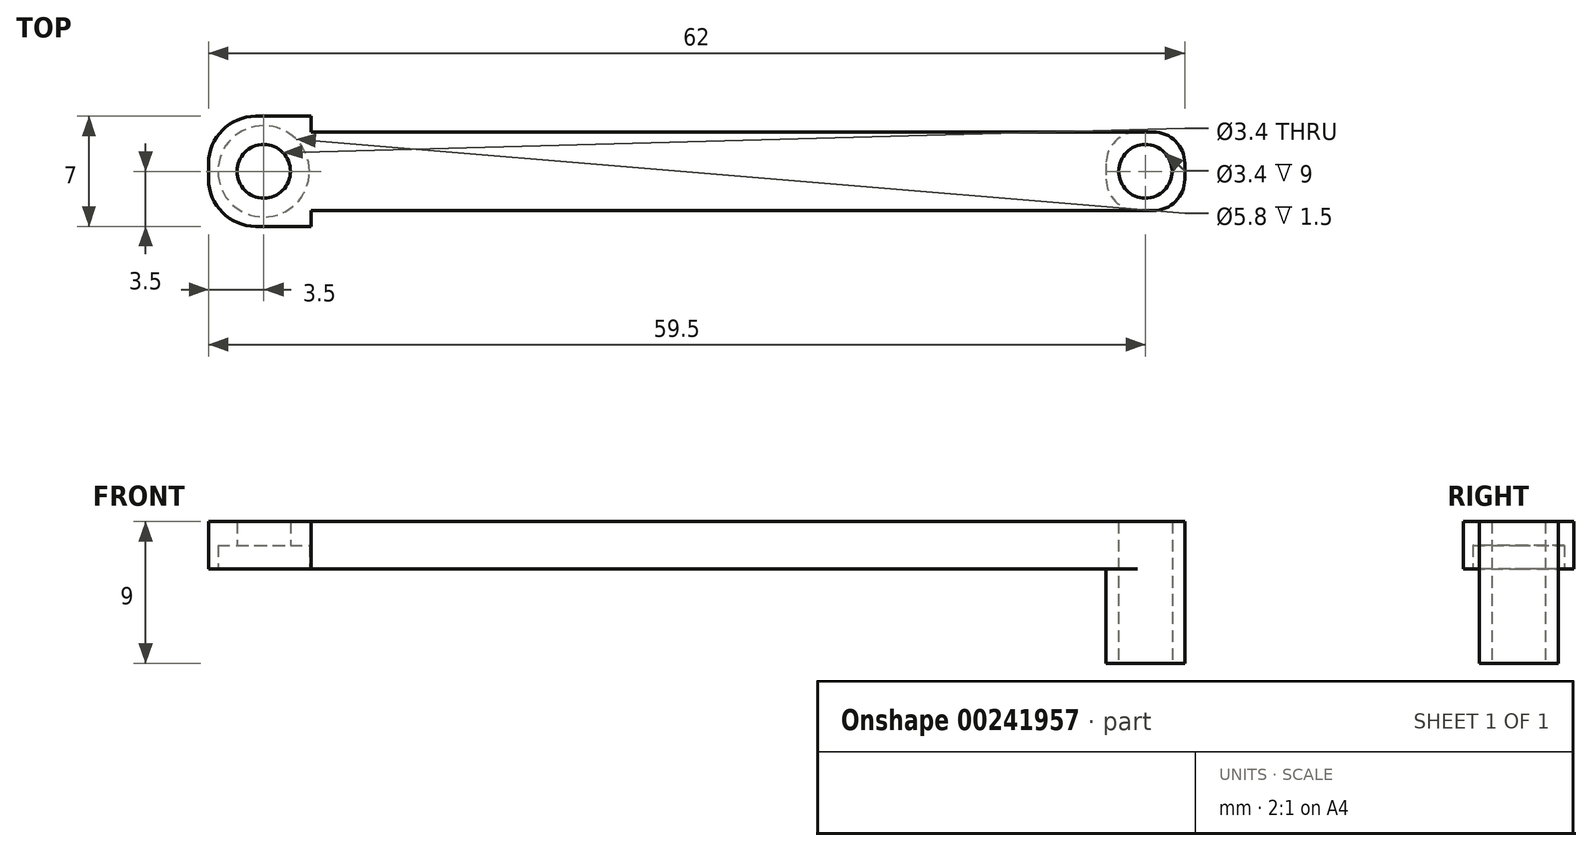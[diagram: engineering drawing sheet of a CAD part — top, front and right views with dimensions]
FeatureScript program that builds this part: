
annotation { "Feature Type Name" : "Feature", "Feature Type Description" : "" }
export const myFeature = defineFeature(function(context is Context, id is Id, definition is map)
    precondition{}
    {
        {
            var Q0;
            Q0=qCreatedBy(makeId("Top.planeOp"),FACE);
            var sketch = newSketch(context, id + "F0", { "sketchPlane" : qUnion([Q0])});
            skCircle(sketch, "E0", {"center": v(0, 0) * mm, "radius": 1.7 * mm});
            skCircle(sketch, "E1", {"center": v(56, 0) * mm, "radius": 1.7 * mm});
            skLineSegment(sketch, "E2", {"start": v(0, 0) * mm, "end": v(56, 0) * mm, "construction": true});
            skLineSegment(sketch, "E3", {"start": v(-2.5, 0) * mm, "end": v(-2.5, 2.5) * mm});
            skLineSegment(sketch, "E4", {"start": v(-2.5, 2.5) * mm, "end": v(58.5, 2.5) * mm});
            skLineSegment(sketch, "E5", {"start": v(58.5, 2.5) * mm, "end": v(58.5, 0) * mm});
            skLineSegment(sketch, "E6.MirrorCS", {"start": v(-2.5, 0) * mm, "end": v(-2.5, -2.5) * mm});
            skLineSegment(sketch, "E7.MirrorCS", {"start": v(-2.5, -2.5) * mm, "end": v(58.5, -2.5) * mm});
            skLineSegment(sketch, "E8.MirrorCS", {"start": v(58.5, -2.5) * mm, "end": v(58.5, 0) * mm});
            skSolve(sketch);
        }
        {
            var Q0;
            Q0=makeQuery(id+"F0.imprint","IMPRINT",FACE,{"disambiguationData":[TD([[makeQuery(id+"F0.imprint","IMPRINT",EDGE,{"derivedFrom":sQuery(id+"F0.wireOp",EDGE,"E0")}),-1.0]])]});
            extrude(context, id + "F1", {"entities" : qUnion([Q0]), "depth" : 3 * mm});
        }
        {
            var Q0;
            Q0=makeQuery(id+"F1.opExtrude","SWEPT_EDGE",EDGE,{"disambiguationData":[OSD([sQuery(id+"F0.wireOp",EDGE,"E3"),sQuery(id+"F0.wireOp",EDGE,"E4")])]});
            var Q1;
            Q1=makeQuery(id+"F1.opExtrude","SWEPT_EDGE",EDGE,{"disambiguationData":[OSD([sQuery(id+"F0.wireOp",EDGE,"E6.MirrorCS"),sQuery(id+"F0.wireOp",EDGE,"E7.MirrorCS")])]});
            var Q2;
            Q2=makeQuery(id+"F1.opExtrude","SWEPT_EDGE",EDGE,{"disambiguationData":[OSD([sQuery(id+"F0.wireOp",EDGE,"E4"),sQuery(id+"F0.wireOp",EDGE,"E5")])]});
            var Q3;
            Q3=makeQuery(id+"F1.opExtrude","SWEPT_EDGE",EDGE,{"disambiguationData":[OSD([sQuery(id+"F0.wireOp",EDGE,"E7.MirrorCS"),sQuery(id+"F0.wireOp",EDGE,"E8.MirrorCS")])]});
            fillet(context, id + "F2", {"entities" : qUnion([Q0, Q1, Q2, Q3]), "radius" : 2 * mm, "tangentPropagation" : true, "allowEdgeOverflow" : false});
        }
        {
            var Q0;
            Q0=makeQuery(id+"F1.opExtrude","CAP_FACE",FACE,{"disambiguationData":[OSD([sQuery(id+"F0.wireOp",EDGE,"E0"),sQuery(id+"F0.wireOp",EDGE,"E1"),sQuery(id+"F0.wireOp",EDGE,"E3"),sQuery(id+"F0.wireOp",EDGE,"E4"),sQuery(id+"F0.wireOp",EDGE,"E5"),sQuery(id+"F0.wireOp",EDGE,"E6.MirrorCS"),sQuery(id+"F0.wireOp",EDGE,"E7.MirrorCS"),sQuery(id+"F0.wireOp",EDGE,"E8.MirrorCS")])],"isStart":true});
            var sketch = newSketch(context, id + "F3", { "sketchPlane" : qUnion([Q0])});
            skArc(sketch, "E9.0", {"start": v(56.5, -2.5) * mm, "mid": v(57.91, -1.91) * mm, "end": v(58.5, -0.5) * mm});
            skPoint(sketch, "E10.0", {"position": v(58.5, 0) * mm});
            skPoint(sketch, "E11.0", {"position": v(57.91, 1.91) * mm});
            skArc(sketch, "E12.0", {"start": v(58.5, 0.5) * mm, "mid": v(57.91, 1.91) * mm, "end": v(56.5, 2.5) * mm});
            skLineSegment(sketch, "E13", {"start": v(56.5, -2.5) * mm, "end": v(53.5, -2.5) * mm});
            skLineSegment(sketch, "E14", {"start": v(53.5, -2.5) * mm, "end": v(53.5, 2.5) * mm});
            skLineSegment(sketch, "E15", {"start": v(53.5, 2.5) * mm, "end": v(56.5, 2.5) * mm});
            skCircle(sketch, "E16.0", {"center": v(56, 0) * mm, "radius": 1.7 * mm});
            skSolve(sketch);
        }
        {
            var Q0;
            Q0=makeQuery(id+"F3.imprint","IMPRINT",FACE,{"disambiguationData":[TD([[makeQuery(id+"F3.imprint","IMPRINT",EDGE,{"derivedFrom":sQuery(id+"F3.wireOp",EDGE,"E9.0")}),1.0]])]});
            extrude(context, id + "F4", {"entities" : qUnion([Q0]), "operationType" : NewBodyOperationType.ADD, "depth" : 6 * mm});
        }
        {
            var Q0;
            Q0=makeQuery(id+"F4.opExtrude","SWEPT_EDGE",EDGE,{"disambiguationData":[OSD([sQuery(id+"F0.wireOp",EDGE,"E4"),sQuery(id+"F3.wireOp",EDGE,"E13"),sQuery(id+"F3.wireOp",EDGE,"E14")])]});
            var Q1;
            Q1=makeQuery(id+"F4.opExtrude","SWEPT_EDGE",EDGE,{"disambiguationData":[OSD([sQuery(id+"F0.wireOp",EDGE,"E7.MirrorCS"),sQuery(id+"F3.wireOp",EDGE,"E14"),sQuery(id+"F3.wireOp",EDGE,"E15")])]});
            fillet(context, id + "F5", {"entities" : qUnion([Q0, Q1]), "radius" : 2 * mm, "tangentPropagation" : true, "allowEdgeOverflow" : false});
        }
        {
            var Q0;
            Q0=makeQuery(id+"F1.opExtrude","CAP_FACE",FACE,{"disambiguationData":[OSD([sQuery(id+"F0.wireOp",EDGE,"E0"),sQuery(id+"F0.wireOp",EDGE,"E1"),sQuery(id+"F0.wireOp",EDGE,"E3"),sQuery(id+"F0.wireOp",EDGE,"E4"),sQuery(id+"F0.wireOp",EDGE,"E5"),sQuery(id+"F0.wireOp",EDGE,"E6.MirrorCS"),sQuery(id+"F0.wireOp",EDGE,"E7.MirrorCS"),sQuery(id+"F0.wireOp",EDGE,"E8.MirrorCS")])],"isStart":false});
            var sketch = newSketch(context, id + "F6", { "sketchPlane" : qUnion([Q0])});
            skCircle(sketch, "E17.0", {"center": v(0, 0) * mm, "radius": 1.7 * mm});
            skArc(sketch, "E17.1", {"start": v(-0.5, 2.5) * mm, "mid": v(-1.91, 1.91) * mm, "end": v(-2.5, 0.5) * mm});
            skArc(sketch, "E17.2", {"start": v(-2.5, -0.5) * mm, "mid": v(-1.91, -1.91) * mm, "end": v(-0.5, -2.5) * mm});
            skCircle(sketch, "E17.4", {"center": v(0, 0) * mm, "radius": 1.7 * mm});
            skArc(sketch, "E17.5", {"start": v(-2.5, 0.5) * mm, "mid": v(-1.91, 1.91) * mm, "end": v(-0.5, 2.5) * mm});
            skArc(sketch, "E17.6", {"start": v(-0.5, -2.5) * mm, "mid": v(-1.91, -1.91) * mm, "end": v(-2.5, -0.5) * mm});
            skLineSegment(sketch, "E17.8", {"start": v(-2.5, -0.5) * mm, "end": v(-2.5, 0.5) * mm});
            skLineSegment(sketch, "E17.11", {"start": v(-2.5, -0.5) * mm, "end": v(-2.5, 0.5) * mm});
            skArc(sketch, "E18.0", {"start": v(-3.5, 0.5) * mm, "mid": v(-2.62, 2.62) * mm, "end": v(-0.5, 3.5) * mm});
            skLineSegment(sketch, "E18.1", {"start": v(-3.5, -0.5) * mm, "end": v(-3.5, 0.5) * mm});
            skArc(sketch, "E18.2", {"start": v(-0.5, -3.5) * mm, "mid": v(-2.62, -2.62) * mm, "end": v(-3.5, -0.5) * mm});
            skLineSegment(sketch, "E19", {"start": v(-0.5, 3.5) * mm, "end": v(3, 3.5) * mm});
            skLineSegment(sketch, "E20", {"start": v(3, 3.5) * mm, "end": v(3, 2.5) * mm});
            skLineSegment(sketch, "E21", {"start": v(3, 2.5) * mm, "end": v(3, -2.5) * mm});
            skLineSegment(sketch, "E22", {"start": v(-0.5, -3.5) * mm, "end": v(3, -3.5) * mm});
            skLineSegment(sketch, "E23", {"start": v(3, -3.5) * mm, "end": v(3, -2.5) * mm});
            skSolve(sketch);
        }
        {
            var Q0;
            Q0 = qSketchRegion(id + "F6", true);
            var Q1;
            Q1=makeQuery(id+"F1.opExtrude","CAP_FACE",FACE,{"disambiguationData":[OSD([sQuery(id+"F0.wireOp",EDGE,"E0"),sQuery(id+"F0.wireOp",EDGE,"E1"),sQuery(id+"F0.wireOp",EDGE,"E3"),sQuery(id+"F0.wireOp",EDGE,"E4"),sQuery(id+"F0.wireOp",EDGE,"E5"),sQuery(id+"F0.wireOp",EDGE,"E6.MirrorCS"),sQuery(id+"F0.wireOp",EDGE,"E7.MirrorCS"),sQuery(id+"F0.wireOp",EDGE,"E8.MirrorCS")])],"isStart":true});
            extrude(context, id + "F7", {"entities" : qUnion([Q0]), "operationType" : NewBodyOperationType.ADD, "endBound" : BoundingType.UP_TO_SURFACE, "oppositeDirection" : true, "endBoundEntityFace" : qUnion([Q1]), "depth" : 25 * mm});
        }
        {
            var Q0;
            Q0=makeQuery(id+"F7.boolean.opBoolean","MERGE",FACE,{"derivedFrom":[makeQuery(id+"F1.opExtrude","CAP_FACE",FACE,{"disambiguationData":[OSD([sQuery(id+"F0.wireOp",EDGE,"E0"),sQuery(id+"F0.wireOp",EDGE,"E1"),sQuery(id+"F0.wireOp",EDGE,"E3"),sQuery(id+"F0.wireOp",EDGE,"E4"),sQuery(id+"F0.wireOp",EDGE,"E5"),sQuery(id+"F0.wireOp",EDGE,"E6.MirrorCS"),sQuery(id+"F0.wireOp",EDGE,"E7.MirrorCS"),sQuery(id+"F0.wireOp",EDGE,"E8.MirrorCS")])],"isStart":true}),makeQuery(id+"F7.opExtrude","CAP_FACE",FACE,{"disambiguationData":[OSD([sQuery(id+"F6.wireOp",EDGE,"E17.4"),sQuery(id+"F6.wireOp",EDGE,"E18.0"),sQuery(id+"F6.wireOp",EDGE,"E18.1"),sQuery(id+"F6.wireOp",EDGE,"E18.2"),sQuery(id+"F6.wireOp",EDGE,"E19"),sQuery(id+"F6.wireOp",EDGE,"E20"),sQuery(id+"F6.wireOp",EDGE,"E21"),sQuery(id+"F6.wireOp",EDGE,"E22"),sQuery(id+"F6.wireOp",EDGE,"E23")])],"isStart":false})]});
            var sketch = newSketch(context, id + "F8", { "sketchPlane" : qUnion([Q0])});
            skCircle(sketch, "E24.0", {"center": v(0, 0) * mm, "radius": 2.9 * mm});
            skSolve(sketch);
        }
        {
            var Q0;
            Q0 = qSketchRegion(id + "F8", true);
            extrude(context, id + "F9", {"entities" : qUnion([Q0]), "operationType" : NewBodyOperationType.REMOVE, "oppositeDirection" : true, "depth" : 1.5 * mm});
        }
    });
